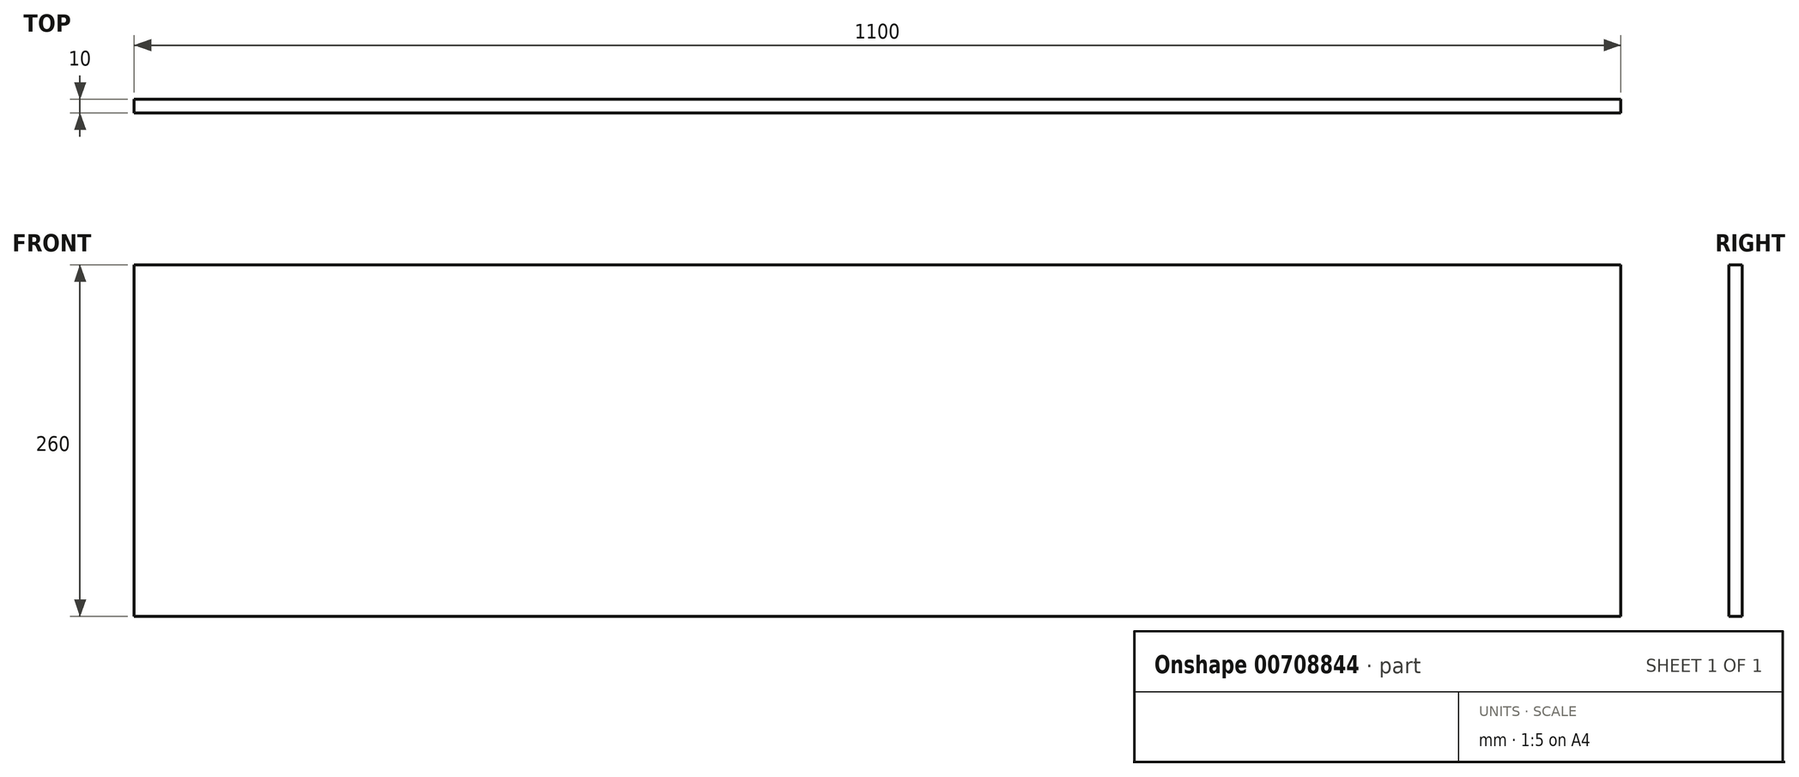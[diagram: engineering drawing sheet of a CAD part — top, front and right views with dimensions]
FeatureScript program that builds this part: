
annotation { "Feature Type Name" : "Feature", "Feature Type Description" : "" }
export const myFeature = defineFeature(function(context is Context, id is Id, definition is map)
    precondition{}
    {
        {
            var Q0;
            Q0=qCreatedBy(makeId("Front.planeOp"),FACE);
            var sketch = newSketch(context, id + "F0", { "sketchPlane" : qUnion([Q0])});
            skLineSegment(sketch, "E0.bottom", {"start": v(0, 0) * mm, "end": v(1100, 0) * mm});
            skLineSegment(sketch, "E0.top", {"start": v(0, 260) * mm, "end": v(1100, 260) * mm});
            skLineSegment(sketch, "E0.left", {"start": v(0, 0) * mm, "end": v(0, 260) * mm});
            skLineSegment(sketch, "E0.right", {"start": v(1100, 0) * mm, "end": v(1100, 260) * mm});
            skSolve(sketch);
        }
        {
            var Q0;
            Q0 = qSketchRegion(id + "F0", true);
            extrude(context, id + "F1", {"entities" : qUnion([Q0]), "depth" : 10 * mm, "offsetDistance" : 25 * mm});
        }
    });
